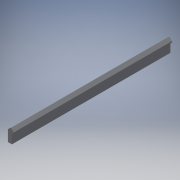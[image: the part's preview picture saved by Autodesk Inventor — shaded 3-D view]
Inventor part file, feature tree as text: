
AUTODESK INVENTOR PART (.ipt)
format: ipt  version: 2017.1 (Build 211199000, 199)  size: 117,248 bytes
history: native  units: in
note: dims shown in document units (in); Inventor stores cm internally (conversion verified against a paired STEP export)
features: fillet x1, other x1, imported_body x1
ambient origin geometry x8: Origin, YZ Plane, XZ Plane, XY Plane, X Axis, Y Axis, Z Axis, Center Point
bodies: Body1 (feature_tree)
feature tree (3):
  fillet  "Fillet1"  [1 undecoded]
  other  "BWC-T4-11"
  imported_body  "Base1"
note: 1 required parameter value undecoded (feature->parameter linkage not recoverable at this tier; creation-order binding heuristic only, values carry confidence <= 0.55)
